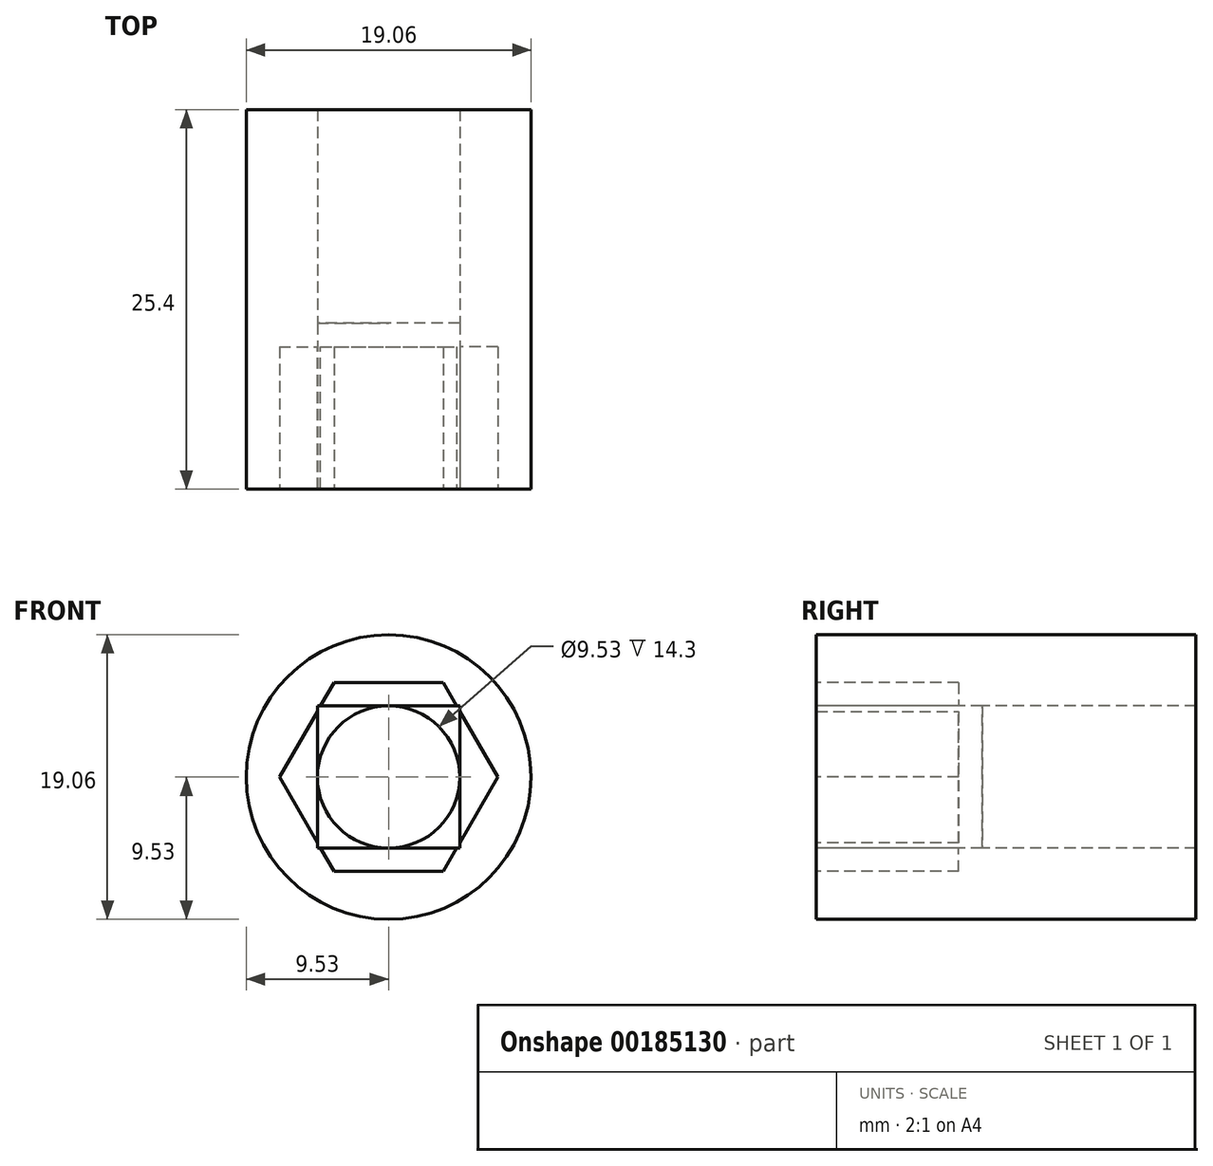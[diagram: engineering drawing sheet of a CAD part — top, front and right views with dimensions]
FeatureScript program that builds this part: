
annotation { "Feature Type Name" : "Feature", "Feature Type Description" : "" }
export const myFeature = defineFeature(function(context is Context, id is Id, definition is map)
    precondition{}
    {
        {
            var Q0;
            Q0=qCreatedBy(makeId("Front.planeOp"),FACE);
            var sketch = newSketch(context, id + "F0", { "sketchPlane" : qUnion([Q0])});
            skCircle(sketch, "E0", {"center": v(0, 0) * mm, "radius": 9.53 * mm});
            skSolve(sketch);
        }
        {
            var Q0;
            Q0 = qSketchRegion(id + "F0", true);
            extrude(context, id + "F1", {"entities" : qUnion([Q0]), "oppositeDirection" : true, "depth" : 25.4 * mm});
        }
        {
            var Q0;
            Q0=qCreatedBy(makeId("Front.planeOp"),FACE);
            var sketch = newSketch(context, id + "F2", { "sketchPlane" : qUnion([Q0])});
            skLineSegment(sketch, "E1.bottom", {"start": v(4.76, -4.76) * mm, "end": v(-4.76, -4.76) * mm});
            skLineSegment(sketch, "E1.top", {"start": v(4.76, 4.76) * mm, "end": v(-4.76, 4.76) * mm});
            skLineSegment(sketch, "E1.left", {"start": v(4.76, -4.76) * mm, "end": v(4.76, 4.76) * mm});
            skLineSegment(sketch, "E1.right", {"start": v(-4.76, -4.76) * mm, "end": v(-4.76, 4.76) * mm});
            skPoint(sketch, "E1.middle", {"position": v(0, 0) * mm});
            skCircle(sketch, "E2", {"center": v(0, 0) * mm, "radius": 4.76 * mm});
            skSolve(sketch);
        }
        {
            var Q0;
            {var subQ0=sQuery(id+"F2.wireOp",EDGE,"E2");var subQ1=makeQuery(id+"F2.imprint","INTERSECT",VERTEX,{"derivedFrom":[sQuery(id+"F2.wireOp",EDGE,"E1.top"),subQ0]});Q0=makeQuery(id+"F2.imprint","IMPRINT",FACE,{"disambiguationData":[TD([[makeQuery(id+"F2.imprint","IMPRINT",EDGE,{"disambiguationData":[TD([[subQ1,1.0]])],"derivedFrom":subQ0}),1.0]])]});}
            extrude(context, id + "F3", {"entities" : qUnion([Q0]), "operationType" : NewBodyOperationType.REMOVE, "endBound" : BoundingType.THROUGH_ALL, "oppositeDirection" : true, "depth" : 25.4 * mm});
        }
        {
            var Q0;
            Q0 = qSketchRegion(id + "F2", true);
            extrude(context, id + "F4", {"entities" : qUnion([Q0]), "operationType" : NewBodyOperationType.REMOVE, "oppositeDirection" : true, "depth" : 11.1 * mm});
        }
        {
            var Q0;
            Q0=qCreatedBy(makeId("Front.planeOp"),FACE);
            var sketch = newSketch(context, id + "F5", { "sketchPlane" : qUnion([Q0])});
            skCircle(sketch, "E3.cCircle", {"center": v(0, 0) * mm, "radius": 7.3 * mm, "construction": true});
            skLineSegment(sketch, "E3.0", {"start": v(7.3, 0) * mm, "end": v(3.65, -6.32) * mm});
            skLineSegment(sketch, "E3.1", {"start": v(3.65, -6.32) * mm, "end": v(-3.65, -6.32) * mm});
            skLineSegment(sketch, "E3.2", {"start": v(-3.65, -6.32) * mm, "end": v(-7.3, 0) * mm});
            skLineSegment(sketch, "E3.3", {"start": v(-7.3, 0) * mm, "end": v(-3.65, 6.32) * mm});
            skLineSegment(sketch, "E3.4", {"start": v(-3.65, 6.32) * mm, "end": v(3.65, 6.32) * mm});
            skLineSegment(sketch, "E3.5", {"start": v(3.65, 6.32) * mm, "end": v(7.3, 0) * mm});
            skSolve(sketch);
        }
        {
            var Q0;
            Q0 = qSketchRegion(id + "F5", true);
            extrude(context, id + "F6", {"entities" : qUnion([Q0]), "operationType" : NewBodyOperationType.REMOVE, "oppositeDirection" : true, "depth" : 9.52 * mm});
        }
    });
